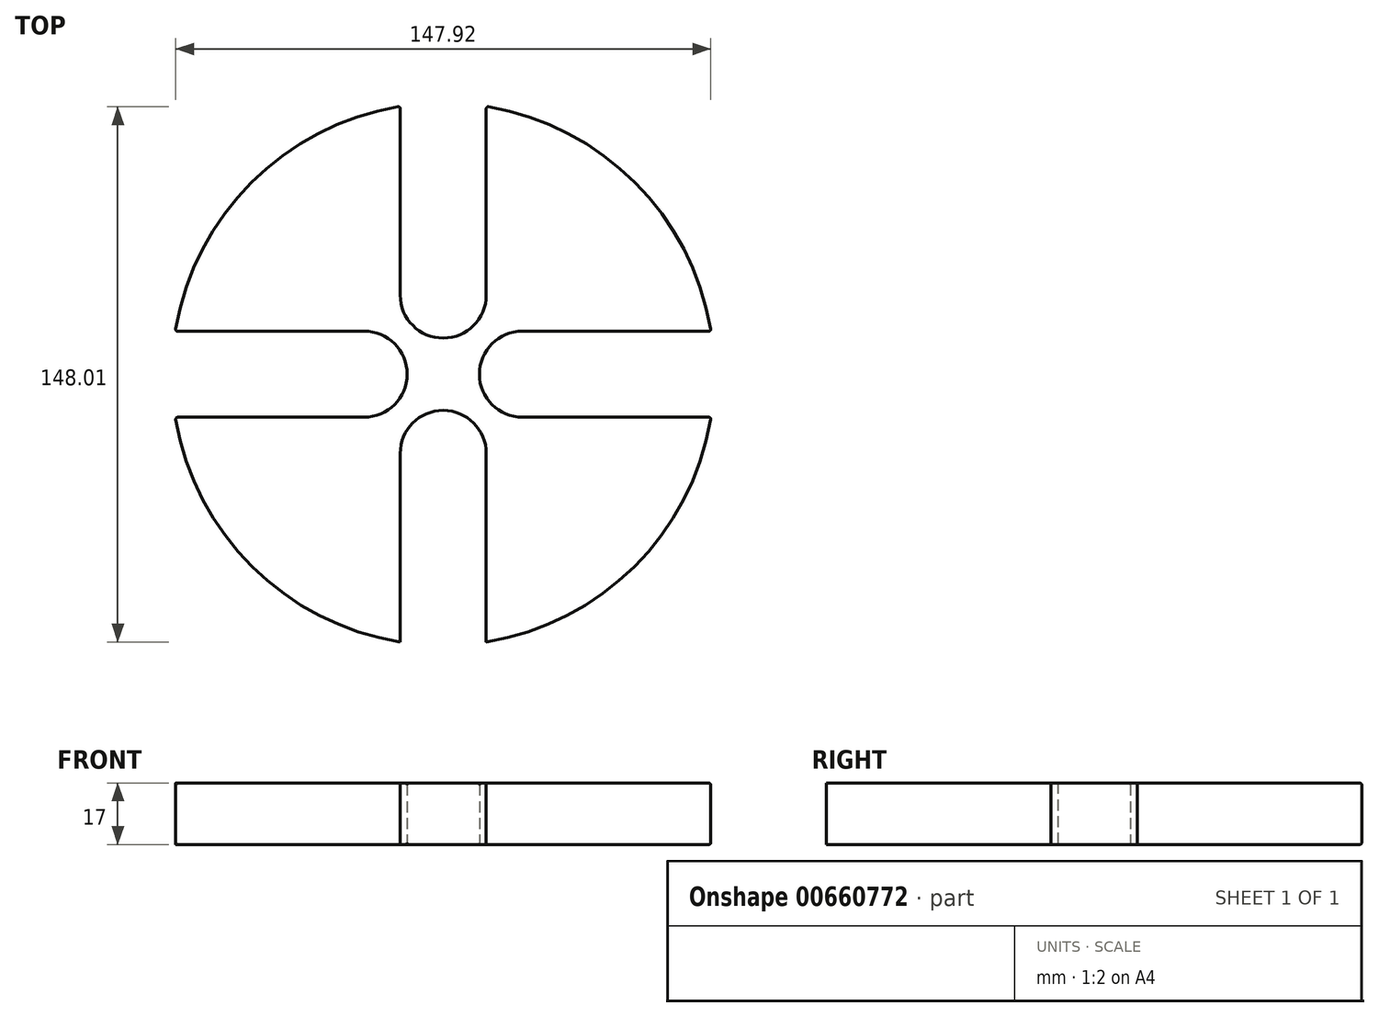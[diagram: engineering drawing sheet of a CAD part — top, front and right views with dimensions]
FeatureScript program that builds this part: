
annotation { "Feature Type Name" : "Feature", "Feature Type Description" : "" }
export const myFeature = defineFeature(function(context is Context, id is Id, definition is map)
    precondition{}
    {
        {
            var Q0;
            Q0=qCreatedBy(makeId("Top.planeOp"),FACE);
            var sketch = newSketch(context, id + "F0", { "sketchPlane" : qUnion([Q0])});
            skCircle(sketch, "E0", {"center": v(0, 0) * mm, "radius": 75 * mm});
            skLineSegment(sketch, "E1", {"start": v(0, 0) * mm, "end": v(75, 0) * mm});
            skArc(sketch, "E2", {"start": v(21.9, 11.9) * mm, "mid": v(10, 0) * mm, "end": v(21.9, -11.9) * mm});
            skLineSegment(sketch, "E3", {"start": v(21.9, 11.9) * mm, "end": v(74.05, 11.9) * mm});
            skLineSegment(sketch, "E4", {"start": v(21.9, -11.9) * mm, "end": v(74.05, -11.9) * mm});
            skLineSegment(sketch, "E5.1.0", {"start": v(-11.9, 21.9) * mm, "end": v(-11.9, 74.05) * mm});
            skArc(sketch, "E5.1.1", {"start": v(-11.9, 21.9) * mm, "mid": v(0, 10) * mm, "end": v(11.9, 21.9) * mm});
            skLineSegment(sketch, "E5.1.2", {"start": v(11.9, 21.9) * mm, "end": v(11.9, 74.05) * mm});
            skLineSegment(sketch, "E5.2.0", {"start": v(-21.9, -11.9) * mm, "end": v(-74.05, -11.9) * mm});
            skArc(sketch, "E5.2.1", {"start": v(-21.9, -11.9) * mm, "mid": v(-10, 0) * mm, "end": v(-21.9, 11.9) * mm});
            skLineSegment(sketch, "E5.2.2", {"start": v(-21.9, 11.9) * mm, "end": v(-74.05, 11.9) * mm});
            skLineSegment(sketch, "E6.1.3.0", {"start": v(11.9, -21.9) * mm, "end": v(11.9, -74.05) * mm});
            skArc(sketch, "E6.3.3.0", {"start": v(11.9, -21.9) * mm, "mid": v(0, -10) * mm, "end": v(-11.9, -21.9) * mm});
            skLineSegment(sketch, "E6.7.3.0", {"start": v(-11.9, -21.9) * mm, "end": v(-11.9, -74.05) * mm});
            skCircle(sketch, "E7", {"center": v(0, 0) * mm, "radius": 10 * mm, "construction": true});
            skSolve(sketch);
        }
        {
            var Q0;
            {var subQ1=sQuery(id+"F0.wireOp",EDGE,"E3");Q0=makeQuery(id+"F0.imprint","IMPRINT",FACE,{"disambiguationData":[TD([[makeQuery(id+"F0.imprint","IMPRINT",EDGE,{"derivedFrom":subQ1}),1.0]])]});}
            extrude(context, id + "F1", {"entities" : qUnion([Q0]), "depth" : 17 * mm, "offsetDistance" : 25 * mm});
        }
        {
            var Q0;
            Q0=makeQuery(id+"F1.opExtrude","CAP_EDGE",EDGE,{"disambiguationData":[OSD([sQuery(id+"F0.wireOp",EDGE,"E3")])],"isStart":true});
            var Q1;
            Q1=makeQuery(id+"F1.opExtrude","CAP_EDGE",EDGE,{"disambiguationData":[OSD([sQuery(id+"F0.wireOp",EDGE,"E5.1.2")])],"isStart":true});
            var Q2;
            Q2=makeQuery(id+"F1.opExtrude","CAP_EDGE",EDGE,{"disambiguationData":[OSD([sQuery(id+"F0.wireOp",EDGE,"E5.2.2")])],"isStart":true});
            var Q3;
            Q3=makeQuery(id+"F1.opExtrude","CAP_EDGE",EDGE,{"disambiguationData":[OSD([sQuery(id+"F0.wireOp",EDGE,"E5.2.0")])],"isStart":false});
            var Q4;
            Q4=makeQuery(id+"F1.opExtrude","CAP_EDGE",EDGE,{"disambiguationData":[OSD([sQuery(id+"F0.wireOp",EDGE,"E5.1.2")])],"isStart":false});
            var Q5;
            Q5=makeQuery(id+"F1.opExtrude","CAP_EDGE",EDGE,{"disambiguationData":[OSD([sQuery(id+"F0.wireOp",EDGE,"E3")])],"isStart":false});
            var Q6;
            {var subQ0=sQuery(id+"F0.wireOp",EDGE,"E0");Q6=makeQuery(id+"F1.opExtrude","CAP_EDGE",EDGE,{"disambiguationData":[OSD([subQ0]),TDD([makeQuery(id+"F0.imprint","IMPRINT",EDGE,{"disambiguationData":[TD([[makeQuery(id+"F0.imprint","INTERSECT",VERTEX,{"derivedFrom":[subQ0,sQuery(id+"F0.wireOp",EDGE,"E5.1.0")]}),-1.0]])],"derivedFrom":subQ0})])],"isStart":false});}
            var Q7;
            {var subQ0=sQuery(id+"F0.wireOp",EDGE,"E0");Q7=makeQuery(id+"F1.opExtrude","CAP_EDGE",EDGE,{"disambiguationData":[OSD([subQ0]),TDD([makeQuery(id+"F0.imprint","IMPRINT",EDGE,{"disambiguationData":[TD([[makeQuery(id+"F0.imprint","INTERSECT",VERTEX,{"derivedFrom":[subQ0,sQuery(id+"F0.wireOp",EDGE,"E4")]}),1.0]])],"derivedFrom":subQ0})])],"isStart":false});}
            var Q8;
            {var subQ0=sQuery(id+"F0.wireOp",EDGE,"E0");Q8=makeQuery(id+"F1.opExtrude","CAP_EDGE",EDGE,{"disambiguationData":[OSD([subQ0]),TDD([makeQuery(id+"F0.imprint","IMPRINT",EDGE,{"disambiguationData":[TD([[makeQuery(id+"F0.imprint","INTERSECT",VERTEX,{"derivedFrom":[subQ0,sQuery(id+"F0.wireOp",EDGE,"E3")]}),-1.0]])],"derivedFrom":subQ0})])],"isStart":false});}
            var Q9;
            {var subQ0=sQuery(id+"F0.wireOp",EDGE,"E0");Q9=makeQuery(id+"F1.opExtrude","CAP_EDGE",EDGE,{"disambiguationData":[OSD([subQ0]),TDD([makeQuery(id+"F0.imprint","IMPRINT",EDGE,{"disambiguationData":[TD([[makeQuery(id+"F0.imprint","INTERSECT",VERTEX,{"derivedFrom":[subQ0,sQuery(id+"F0.wireOp",EDGE,"E4")]}),1.0]])],"derivedFrom":subQ0})])],"isStart":true});}
            var Q10;
            {var subQ0=sQuery(id+"F0.wireOp",EDGE,"E0");Q10=makeQuery(id+"F1.opExtrude","CAP_EDGE",EDGE,{"disambiguationData":[OSD([subQ0]),TDD([makeQuery(id+"F0.imprint","IMPRINT",EDGE,{"disambiguationData":[TD([[makeQuery(id+"F0.imprint","INTERSECT",VERTEX,{"derivedFrom":[subQ0,sQuery(id+"F0.wireOp",EDGE,"E5.1.0")]}),-1.0]])],"derivedFrom":subQ0})])],"isStart":true});}
            var Q11;
            {var subQ0=sQuery(id+"F0.wireOp",EDGE,"E0");Q11=makeQuery(id+"F1.opExtrude","CAP_EDGE",EDGE,{"disambiguationData":[OSD([subQ0]),TDD([makeQuery(id+"F0.imprint","IMPRINT",EDGE,{"disambiguationData":[TD([[makeQuery(id+"F0.imprint","INTERSECT",VERTEX,{"derivedFrom":[subQ0,sQuery(id+"F0.wireOp",EDGE,"E3")]}),-1.0]])],"derivedFrom":subQ0})])],"isStart":true});}
            var Q12;
            Q12=makeQuery(id+"F1.opExtrude","SWEPT_EDGE",EDGE,{"disambiguationData":[OSD([sQuery(id+"F0.wireOp",EDGE,"E0"),sQuery(id+"F0.wireOp",EDGE,"E3")])]});
            var Q13;
            Q13=makeQuery(id+"F1.opExtrude","SWEPT_EDGE",EDGE,{"disambiguationData":[OSD([sQuery(id+"F0.wireOp",EDGE,"E0"),sQuery(id+"F0.wireOp",EDGE,"E4")])]});
            var Q14;
            Q14=makeQuery(id+"F1.opExtrude","SWEPT_EDGE",EDGE,{"disambiguationData":[OSD([sQuery(id+"F0.wireOp",EDGE,"E0"),sQuery(id+"F0.wireOp",EDGE,"E5.2.0")])]});
            var Q15;
            Q15=makeQuery(id+"F1.opExtrude","SWEPT_EDGE",EDGE,{"disambiguationData":[OSD([sQuery(id+"F0.wireOp",EDGE,"E0"),sQuery(id+"F0.wireOp",EDGE,"E5.2.2")])]});
            var Q16;
            Q16=makeQuery(id+"F1.opExtrude","SWEPT_EDGE",EDGE,{"disambiguationData":[OSD([sQuery(id+"F0.wireOp",EDGE,"E0"),sQuery(id+"F0.wireOp",EDGE,"E5.1.2")])]});
            var Q17;
            Q17=makeQuery(id+"F1.opExtrude","SWEPT_EDGE",EDGE,{"disambiguationData":[OSD([sQuery(id+"F0.wireOp",EDGE,"E0"),sQuery(id+"F0.wireOp",EDGE,"E5.1.0")])]});
            fillet(context, id + "F2", {"entities" : qUnion([Q0, Q1, Q2, Q3, Q4, Q5, Q6, Q7, Q8, Q9, Q10, Q11, Q12, Q13, Q14, Q15, Q16, Q17]), "radius" : 0.5 * mm, "tangentPropagation" : true, "allowEdgeOverflow" : false});
        }
    });
